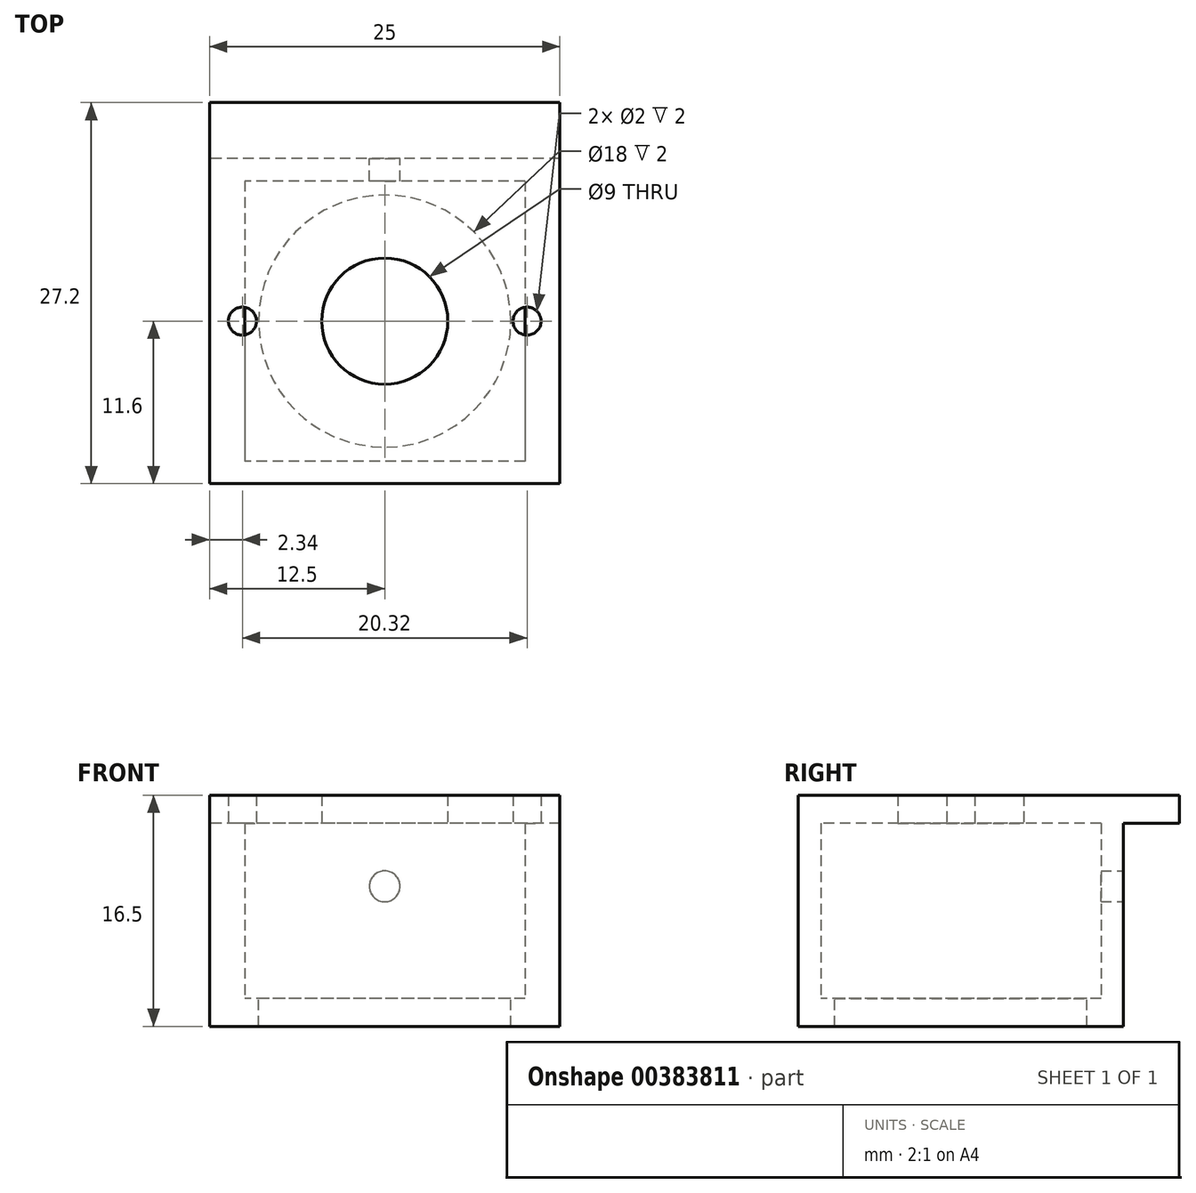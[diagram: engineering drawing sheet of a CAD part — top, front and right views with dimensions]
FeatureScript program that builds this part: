
annotation { "Feature Type Name" : "Feature", "Feature Type Description" : "" }
export const myFeature = defineFeature(function(context is Context, id is Id, definition is map)
    precondition{}
    {
        {
            var Q0;
            Q0=qCreatedBy(makeId("Top.planeOp"),FACE);
            var sketch = newSketch(context, id + "F0", { "sketchPlane" : qUnion([Q0])});
            skLineSegment(sketch, "E0.bottom", {"start": v(12.07, 9.9) * mm, "end": v(-12.07, 9.9) * mm, "construction": true});
            skLineSegment(sketch, "E0.top", {"start": v(12.07, -9.9) * mm, "end": v(-12.07, -9.9) * mm, "construction": true});
            skLineSegment(sketch, "E0.left", {"start": v(12.07, 9.9) * mm, "end": v(12.07, -9.9) * mm, "construction": true});
            skLineSegment(sketch, "E0.right", {"start": v(-12.07, 9.9) * mm, "end": v(-12.07, -9.9) * mm, "construction": true});
            skPoint(sketch, "E0.middle", {"position": v(0, 0) * mm});
            skLineSegment(sketch, "E1", {"start": v(0, 0) * mm, "end": v(10.16, 0) * mm, "construction": true});
            skLineSegment(sketch, "E2", {"start": v(0, 0) * mm, "end": v(-10.16, 0) * mm, "construction": true});
            skCircle(sketch, "E3", {"center": v(-10.16, 0) * mm, "radius": 1.1 * mm, "construction": true});
            skCircle(sketch, "E4", {"center": v(10.16, 0) * mm, "radius": 1.1 * mm, "construction": true});
            skCircle(sketch, "E5", {"center": v(0, 0) * mm, "radius": 10 * mm});
            skLineSegment(sketch, "E6.bottom", {"start": v(12.5, 11.6) * mm, "end": v(-12.5, 11.6) * mm});
            skLineSegment(sketch, "E6.top", {"start": v(12.5, -11.6) * mm, "end": v(-12.5, -11.6) * mm});
            skLineSegment(sketch, "E6.left", {"start": v(12.5, 11.6) * mm, "end": v(12.5, -11.6) * mm});
            skLineSegment(sketch, "E6.right", {"start": v(-12.5, 11.6) * mm, "end": v(-12.5, -11.6) * mm});
            skCircle(sketch, "E7", {"center": v(0, 0) * mm, "radius": 9 * mm});
            skLineSegment(sketch, "E8.bottom", {"start": v(10, 10) * mm, "end": v(-10, 10) * mm});
            skLineSegment(sketch, "E8.top", {"start": v(10, -10) * mm, "end": v(-10, -10) * mm});
            skLineSegment(sketch, "E8.left", {"start": v(10, 10) * mm, "end": v(10, -10) * mm});
            skLineSegment(sketch, "E8.right", {"start": v(-10, 10) * mm, "end": v(-10, -10) * mm});
            skSolve(sketch);
        }
        {
            var Q0;
            Q0 = qSketchRegion(id + "F0", true);
            var Q1;
            Q1=makeQuery(id+"F0.imprint","IMPRINT",FACE,{"disambiguationData":[TD([[makeQuery(id+"F0.imprint","IMPRINT",EDGE,{"derivedFrom":sQuery(id+"F0.wireOp",EDGE,"E5")}),1.0]])]});
            var Q2;
            {var subQ0=sQuery(id+"F0.wireOp",EDGE,"E8.right");var subQ1=sQuery(id+"F0.wireOp",EDGE,"E5");var subQ2=makeQuery(id+"F0.imprint","INTERSECT",VERTEX,{"derivedFrom":[subQ1,subQ0]});Q2=makeQuery(id+"F0.imprint","IMPRINT",FACE,{"disambiguationData":[TD([[makeQuery(id+"F0.imprint","IMPRINT",EDGE,{"disambiguationData":[TD([[subQ2,-1.0]])],"derivedFrom":subQ1}),-1.0]])]});}
            var Q3;
            {var subQ0=sQuery(id+"F0.wireOp",EDGE,"E8.bottom");var subQ1=sQuery(id+"F0.wireOp",EDGE,"E5");var subQ2=makeQuery(id+"F0.imprint","INTERSECT",VERTEX,{"derivedFrom":[subQ1,subQ0]});Q3=makeQuery(id+"F0.imprint","IMPRINT",FACE,{"disambiguationData":[TD([[makeQuery(id+"F0.imprint","IMPRINT",EDGE,{"disambiguationData":[TD([[subQ2,-1.0]])],"derivedFrom":subQ1}),-1.0]])]});}
            var Q4;
            {var subQ0=sQuery(id+"F0.wireOp",EDGE,"E8.bottom");var subQ1=sQuery(id+"F0.wireOp",EDGE,"E5");var subQ2=makeQuery(id+"F0.imprint","INTERSECT",VERTEX,{"derivedFrom":[subQ1,subQ0]});Q4=makeQuery(id+"F0.imprint","IMPRINT",FACE,{"disambiguationData":[TD([[makeQuery(id+"F0.imprint","IMPRINT",EDGE,{"disambiguationData":[TD([[subQ2,1.0]])],"derivedFrom":subQ1}),-1.0]])]});}
            var Q5;
            {var subQ0=sQuery(id+"F0.wireOp",EDGE,"E8.left");var subQ1=sQuery(id+"F0.wireOp",EDGE,"E5");var subQ2=makeQuery(id+"F0.imprint","INTERSECT",VERTEX,{"derivedFrom":[subQ1,subQ0]});Q5=makeQuery(id+"F0.imprint","IMPRINT",FACE,{"disambiguationData":[TD([[makeQuery(id+"F0.imprint","IMPRINT",EDGE,{"disambiguationData":[TD([[subQ2,1.0]])],"derivedFrom":subQ1}),-1.0]])]});}
            extrude(context, id + "F1", {"entities" : qUnion([Q0, Q1, Q2, Q3, Q4, Q5]), "oppositeDirection" : true, "depth" : 2 * mm});
        }
        {
            var Q0;
            Q0=makeQuery(id+"F0.imprint","IMPRINT",FACE,{"disambiguationData":[TD([[makeQuery(id+"F0.imprint","IMPRINT",EDGE,{"derivedFrom":sQuery(id+"F0.wireOp",EDGE,"E6.bottom")}),1.0]])]});
            extrude(context, id + "F2", {"entities" : qUnion([Q0]), "operationType" : NewBodyOperationType.ADD, "depth" : 12.5 * mm});
        }
        {
            var Q0;
            {var subQ0=sQuery(id+"F0.wireOp",EDGE,"E6.bottom");Q0=makeQuery(id+"F2.boolean.opBoolean","MERGE",FACE,{"derivedFrom":[makeQuery(id+"F1.opExtrude","SWEPT_FACE",FACE,{"disambiguationData":[OSD([subQ0])]}),makeQuery(id+"F2.opExtrude","SWEPT_FACE",FACE,{"disambiguationData":[OSD([subQ0])]})]});}
            var sketch = newSketch(context, id + "F3", { "sketchPlane" : qUnion([Q0])});
            skLineSegment(sketch, "E9", {"start": v(0, 12.5) * mm, "end": v(0, 8) * mm});
            skPoint(sketch, "E9.endSnap0", {"position": v(0, 12.5) * mm});
            skCircle(sketch, "E10", {"center": v(0, 8) * mm, "radius": 1.1 * mm});
            skSolve(sketch);
        }
        {
            var Q0;
            Q0 = qSketchRegion(id + "F3", true);
            extrude(context, id + "F4", {"entities" : qUnion([Q0]), "operationType" : NewBodyOperationType.REMOVE, "oppositeDirection" : true, "depth" : 4 * mm});
        }
        {
            var Q0;
            Q0=makeQuery(id+"F2.opExtrude","CAP_FACE",FACE,{"disambiguationData":[OSD([sQuery(id+"F0.wireOp",EDGE,"E6.bottom"),sQuery(id+"F0.wireOp",EDGE,"E6.top"),sQuery(id+"F0.wireOp",EDGE,"E6.left"),sQuery(id+"F0.wireOp",EDGE,"E6.right"),sQuery(id+"F0.wireOp",EDGE,"E8.bottom"),sQuery(id+"F0.wireOp",EDGE,"E8.top"),sQuery(id+"F0.wireOp",EDGE,"E8.left"),sQuery(id+"F0.wireOp",EDGE,"E8.right")])],"isStart":false});
            var sketch = newSketch(context, id + "F5", { "sketchPlane" : qUnion([Q0])});
            skLineSegment(sketch, "E11", {"start": v(0, 0) * mm, "end": v(-10.16, 0) * mm, "construction": true});
            skPoint(sketch, "E11.endSnap0", {"position": v(-10, 0) * mm});
            skLineSegment(sketch, "E12", {"start": v(0, 0) * mm, "end": v(10.16, 0) * mm, "construction": true});
            skCircle(sketch, "E13", {"center": v(10.16, 0) * mm, "radius": 1 * mm});
            skCircle(sketch, "E14", {"center": v(-10.16, 0) * mm, "radius": 1 * mm});
            skCircle(sketch, "E15", {"center": v(0, 0) * mm, "radius": 4.5 * mm});
            skLineSegment(sketch, "E16.bottom", {"start": v(-12.5, -11.6) * mm, "end": v(12.5, -11.6) * mm});
            skLineSegment(sketch, "E16.top", {"start": v(-12.5, 15.6) * mm, "end": v(12.5, 15.6) * mm});
            skLineSegment(sketch, "E16.left", {"start": v(-12.5, -11.6) * mm, "end": v(-12.5, 15.6) * mm});
            skLineSegment(sketch, "E16.right", {"start": v(12.5, -11.6) * mm, "end": v(12.5, 15.6) * mm});
            skLineSegment(sketch, "E17", {"start": v(-12.5, 11.6) * mm, "end": v(-12.5, 15.6) * mm});
            skSolve(sketch);
        }
        {
            var Q0;
            Q0 = qSketchRegion(id + "F5", true);
            extrude(context, id + "F6", {"entities" : qUnion([Q0]), "operationType" : NewBodyOperationType.ADD, "depth" : 2 * mm});
        }
    });
